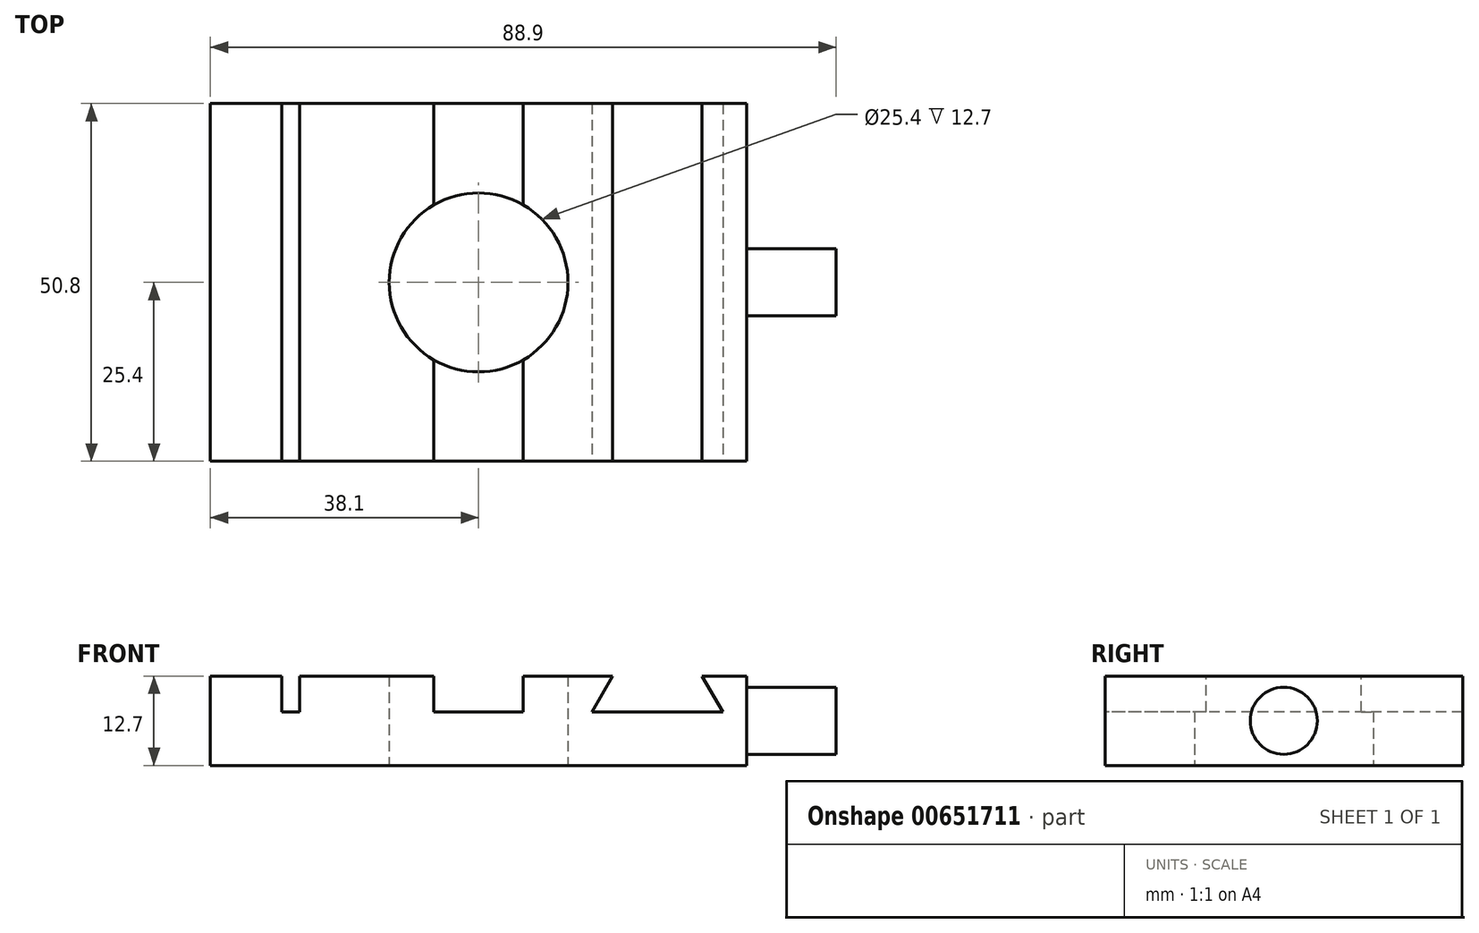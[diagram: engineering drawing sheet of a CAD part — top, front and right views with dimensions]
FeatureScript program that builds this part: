
annotation { "Feature Type Name" : "Feature", "Feature Type Description" : "" }
export const myFeature = defineFeature(function(context is Context, id is Id, definition is map)
    precondition{}
    {
        {
            var Q0;
            Q0=qCreatedBy(makeId("Top.planeOp"),FACE);
            var sketch = newSketch(context, id + "F0", { "sketchPlane" : qUnion([Q0])});
            skLineSegment(sketch, "E0.bottom", {"start": v(38.1, 25.4) * mm, "end": v(-38.1, 25.4) * mm});
            skLineSegment(sketch, "E0.top", {"start": v(38.1, -25.4) * mm, "end": v(-38.1, -25.4) * mm});
            skLineSegment(sketch, "E0.left", {"start": v(38.1, 25.4) * mm, "end": v(38.1, -25.4) * mm});
            skLineSegment(sketch, "E0.right", {"start": v(-38.1, 25.4) * mm, "end": v(-38.1, -25.4) * mm});
            skPoint(sketch, "E0.middle", {"position": v(0, 0) * mm});
            skCircle(sketch, "E1", {"center": v(0, 0) * mm, "radius": 12.7 * mm});
            skSolve(sketch);
        }
        {
            var Q0;
            Q0=makeQuery(id+"F0.imprint","IMPRINT",FACE,{"disambiguationData":[TD([[makeQuery(id+"F0.imprint","IMPRINT",EDGE,{"derivedFrom":sQuery(id+"F0.wireOp",EDGE,"E0.bottom")}),1.0]])]});
            extrude(context, id + "F1", {"entities" : qUnion([Q0]), "depth" : 12.7 * mm, "offsetDistance" : 25.4 * mm});
        }
        {
            var Q0;
            Q0=makeQuery(id+"F1.opExtrude","CAP_FACE",FACE,{"disambiguationData":[OSD([sQuery(id+"F0.wireOp",EDGE,"E0.bottom"),sQuery(id+"F0.wireOp",EDGE,"E0.top"),sQuery(id+"F0.wireOp",EDGE,"E0.left"),sQuery(id+"F0.wireOp",EDGE,"E0.right"),sQuery(id+"F0.wireOp",EDGE,"E1")])],"isStart":false});
            var sketch = newSketch(context, id + "F2", { "sketchPlane" : qUnion([Q0])});
            skLineSegment(sketch, "E2.bottom", {"start": v(-27.94, 25.4) * mm, "end": v(-25.4, 25.4) * mm});
            skLineSegment(sketch, "E2.top", {"start": v(-27.94, -25.4) * mm, "end": v(-25.4, -25.4) * mm});
            skLineSegment(sketch, "E2.left", {"start": v(-27.94, 25.4) * mm, "end": v(-27.94, -25.4) * mm});
            skLineSegment(sketch, "E2.right", {"start": v(-25.4, 25.4) * mm, "end": v(-25.4, -25.4) * mm});
            skLineSegment(sketch, "E3", {"start": v(-6.35, 25.4) * mm, "end": v(-6.35, -25.4) * mm});
            skLineSegment(sketch, "E4", {"start": v(-6.35, -25.4) * mm, "end": v(6.35, -25.4) * mm});
            skLineSegment(sketch, "E5", {"start": v(6.35, -25.4) * mm, "end": v(6.35, 25.4) * mm});
            skLineSegment(sketch, "E6", {"start": v(6.35, 25.4) * mm, "end": v(-6.35, 25.4) * mm});
            skPoint(sketch, "E7", {"position": v(0, 0) * mm});
            skLineSegment(sketch, "E8", {"start": v(0, 25.4) * mm, "end": v(0, -25.4) * mm, "construction": true});
            skSolve(sketch);
        }
        {
            var Q0;
            Q0=makeQuery(id+"F2.imprint","IMPRINT",FACE,{"disambiguationData":[TD([[makeQuery(id+"F2.imprint","IMPRINT",EDGE,{"derivedFrom":sQuery(id+"F2.wireOp",EDGE,"E2.bottom")}),1.0]])]});
            var Q1;
            {var subQ0=sQuery(id+"F2.wireOp",EDGE,"E6");Q1=makeQuery(id+"F2.imprint","IMPRINT",FACE,{"disambiguationData":[TD([[makeQuery(id+"F2.imprint","IMPRINT",EDGE,{"derivedFrom":subQ0}),1.0]])]});}
            var Q2;
            {var subQ0=sQuery(id+"F2.wireOp",EDGE,"E4");Q2=makeQuery(id+"F2.imprint","IMPRINT",FACE,{"disambiguationData":[TD([[makeQuery(id+"F2.imprint","IMPRINT",EDGE,{"derivedFrom":subQ0}),-1.0]])]});}
            extrude(context, id + "F3", {"entities" : qUnion([Q0, Q1, Q2]), "operationType" : NewBodyOperationType.REMOVE, "oppositeDirection" : true, "depth" : 5.08 * mm, "offsetDistance" : 25.4 * mm});
        }
        {
            var Q0;
            Q0=makeQuery(id+"F1.opExtrude","SWEPT_FACE",FACE,{"disambiguationData":[OSD([sQuery(id+"F0.wireOp",EDGE,"E0.top")])]});
            var sketch = newSketch(context, id + "F4", { "sketchPlane" : qUnion([Q0])});
            skLineSegment(sketch, "E9", {"start": v(19.05, 12.7) * mm, "end": v(16.12, 7.62) * mm});
            skLineSegment(sketch, "E10", {"start": v(16.12, 7.62) * mm, "end": v(34.68, 7.62) * mm});
            skLineSegment(sketch, "E11", {"start": v(34.68, 7.62) * mm, "end": v(31.75, 12.7) * mm});
            skLineSegment(sketch, "E12", {"start": v(31.75, 12.7) * mm, "end": v(19.05, 12.7) * mm});
            skLineSegment(sketch, "E13", {"start": v(25.4, 7.62) * mm, "end": v(25.4, 12.7) * mm, "construction": true});
            skSolve(sketch);
        }
        {
            var Q0;
            Q0=makeQuery(id+"F4.imprint","IMPRINT",FACE,{"disambiguationData":[TD([[makeQuery(id+"F4.imprint","IMPRINT",EDGE,{"derivedFrom":sQuery(id+"F4.wireOp",EDGE,"E9")}),1.0]])]});
            extrude(context, id + "F5", {"entities" : qUnion([Q0]), "operationType" : NewBodyOperationType.REMOVE, "endBound" : BoundingType.THROUGH_ALL, "oppositeDirection" : true, "depth" : 25.4 * mm, "offsetDistance" : 25.4 * mm});
        }
        {
            var Q0;
            Q0=makeQuery(id+"F1.opExtrude","SWEPT_FACE",FACE,{"disambiguationData":[OSD([sQuery(id+"F0.wireOp",EDGE,"E0.left")])]});
            var sketch = newSketch(context, id + "F6", { "sketchPlane" : qUnion([Q0])});
            skCircle(sketch, "E14", {"center": v(0, 6.35) * mm, "radius": 4.76 * mm});
            skPoint(sketch, "E14.centerSnap0", {"position": v(-25.4, 6.35) * mm});
            skPoint(sketch, "E14.centerSnap1", {"position": v(0, 12.7) * mm});
            skSolve(sketch);
        }
        {
            var Q0;
            Q0 = qSketchRegion(id + "F6", true);
            extrude(context, id + "F7", {"entities" : qUnion([Q0]), "operationType" : NewBodyOperationType.ADD, "depth" : 12.7 * mm, "offsetDistance" : 25.4 * mm});
        }
    });
